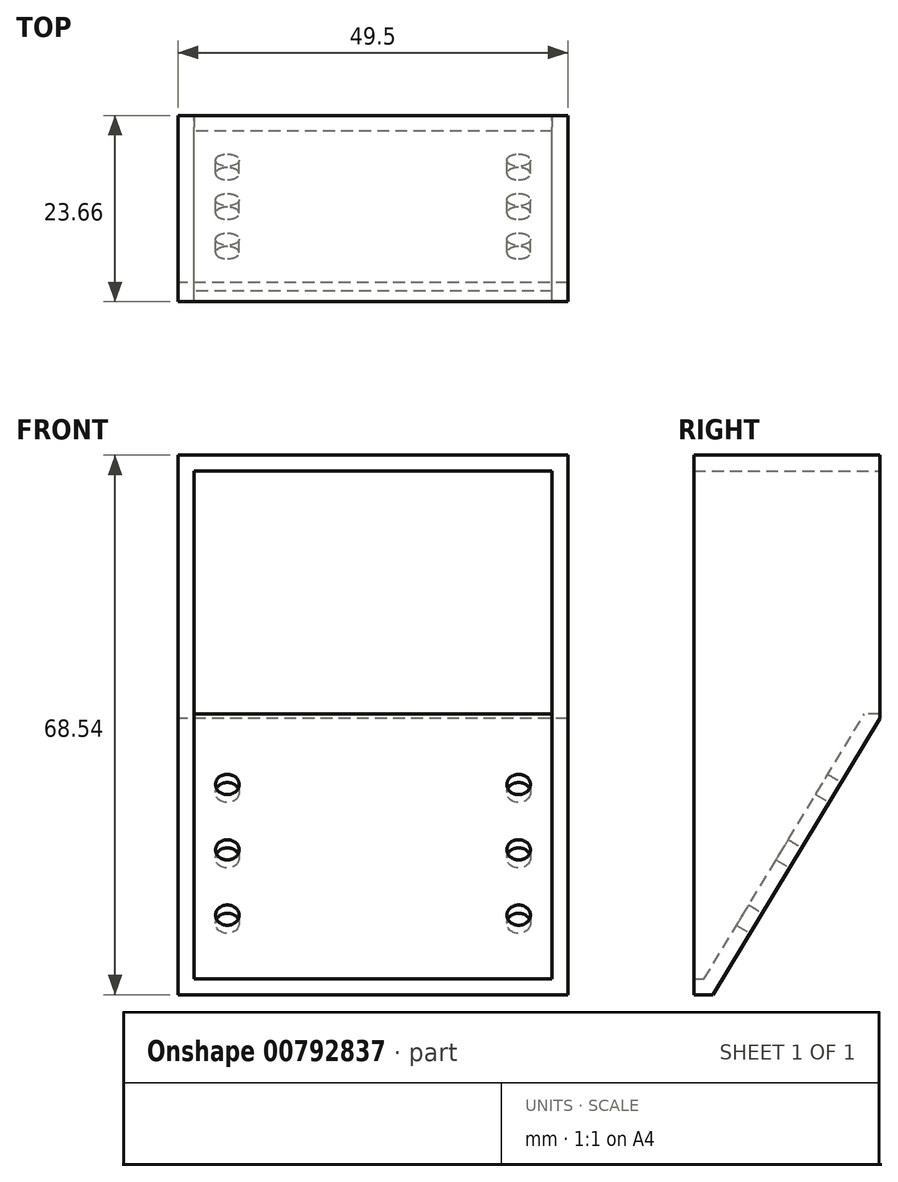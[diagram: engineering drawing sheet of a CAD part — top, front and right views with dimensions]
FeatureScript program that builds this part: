
annotation { "Feature Type Name" : "Feature", "Feature Type Description" : "" }
export const myFeature = defineFeature(function(context is Context, id is Id, definition is map)
    precondition{}
    {
        {
            var Q0;
            Q0=qCreatedBy(makeId("Right.planeOp"),FACE);
            var sketch = newSketch(context, id + "F0", { "sketchPlane" : qUnion([Q0])});
            skLineSegment(sketch, "E0", {"start": v(-9.1, 3.26) * mm, "end": v(14.57, 3.26) * mm});
            skLineSegment(sketch, "E1", {"start": v(14.57, 3.26) * mm, "end": v(14.57, -30.2) * mm});
            skLineSegment(sketch, "E2", {"start": v(-9.1, -65.28) * mm, "end": v(-9.1, 3.26) * mm});
            skLineSegment(sketch, "E3", {"start": v(-9.1, -65.28) * mm, "end": v(-6.64, -65.28) * mm});
            skLineSegment(sketch, "E4", {"start": v(-6.64, -65.28) * mm, "end": v(14.57, -30.2) * mm});
            skSolve(sketch);
        }
        {
            var Q0;
            Q0=qSketchRegion(id+"F0",true);
            extrude(context, id + "F1", {"entities" : qUnion([Q0]), "depth" : 49.5 * mm, "offsetDistance" : 25 * mm});
        }
        {
            var Q0;
            Q0=makeQuery(id+"F1.opExtrude","SWEPT_FACE",FACE,{"disambiguationData":[OSD([sQuery(id+"F0.wireOp",EDGE,"E2")])]});
            shell(context, id + "F2", {"entities" : qUnion([Q0]), "thickness" : 2 * mm});
        }
        {
            var Q0;
            Q0=makeQuery(id+"F2.opShell","OFFSET_FACE",FACE,{"disambiguationData":[OSD([sQuery(id+"F0.wireOp",EDGE,"E1")])]});
            var sketch = newSketch(context, id + "F3", { "sketchPlane" : qUnion([Q0])});
            skLineSegment(sketch, "E5.bottom", {"start": v(2, 1.26) * mm, "end": v(47.5, 1.26) * mm});
            skLineSegment(sketch, "E5.top", {"start": v(2, -29.64) * mm, "end": v(47.5, -29.64) * mm});
            skLineSegment(sketch, "E5.left", {"start": v(2, 1.26) * mm, "end": v(2, -29.64) * mm});
            skLineSegment(sketch, "E5.right", {"start": v(47.5, 1.26) * mm, "end": v(47.5, -29.64) * mm});
            skSolve(sketch);
        }
        {
            var Q0;
            Q0=qSketchRegion(id+"F3",true);
            extrude(context, id + "F4", {"entities" : qUnion([Q0]), "operationType" : NewBodyOperationType.REMOVE, "oppositeDirection" : true, "depth" : 25 * mm, "offsetDistance" : 25 * mm});
        }
        {
            var Q0;
            Q0=makeQuery(id+"F1.opExtrude","SWEPT_FACE",FACE,{"disambiguationData":[OSD([sQuery(id+"F0.wireOp",EDGE,"E4")])]});
            var sketch = newSketch(context, id + "F5", { "sketchPlane" : qUnion([Q0])});
            skLineSegment(sketch, "E6", {"start": v(-24.75, -76.46) * mm, "end": v(-24.75, 28.32) * mm, "construction": true});
            skPoint(sketch, "E6.startSnap0", {"position": v(-24.75, -59.3) * mm});
            skCircle(sketch, "E7", {"center": v(-43.25, -29.3) * mm, "radius": 1.5 * mm});
            skCircle(sketch, "E8", {"center": v(-43.25, -39) * mm, "radius": 1.5 * mm});
            skCircle(sketch, "E9", {"center": v(-43.25, -48.7) * mm, "radius": 1.5 * mm});
            skCircle(sketch, "E10.MirrorC", {"center": v(-6.25, -29.3) * mm, "radius": 1.5 * mm});
            skCircle(sketch, "E11.MirrorC", {"center": v(-6.25, -39) * mm, "radius": 1.5 * mm});
            skCircle(sketch, "E12.MirrorC", {"center": v(-6.25, -48.7) * mm, "radius": 1.5 * mm});
            skSolve(sketch);
        }
        {
            var Q0;
            Q0 = qSketchRegion(id + "F5", true);
            extrude(context, id + "F6", {"entities" : qUnion([Q0]), "operationType" : NewBodyOperationType.REMOVE, "oppositeDirection" : true, "depth" : 25 * mm, "offsetDistance" : 25 * mm});
        }
    });
